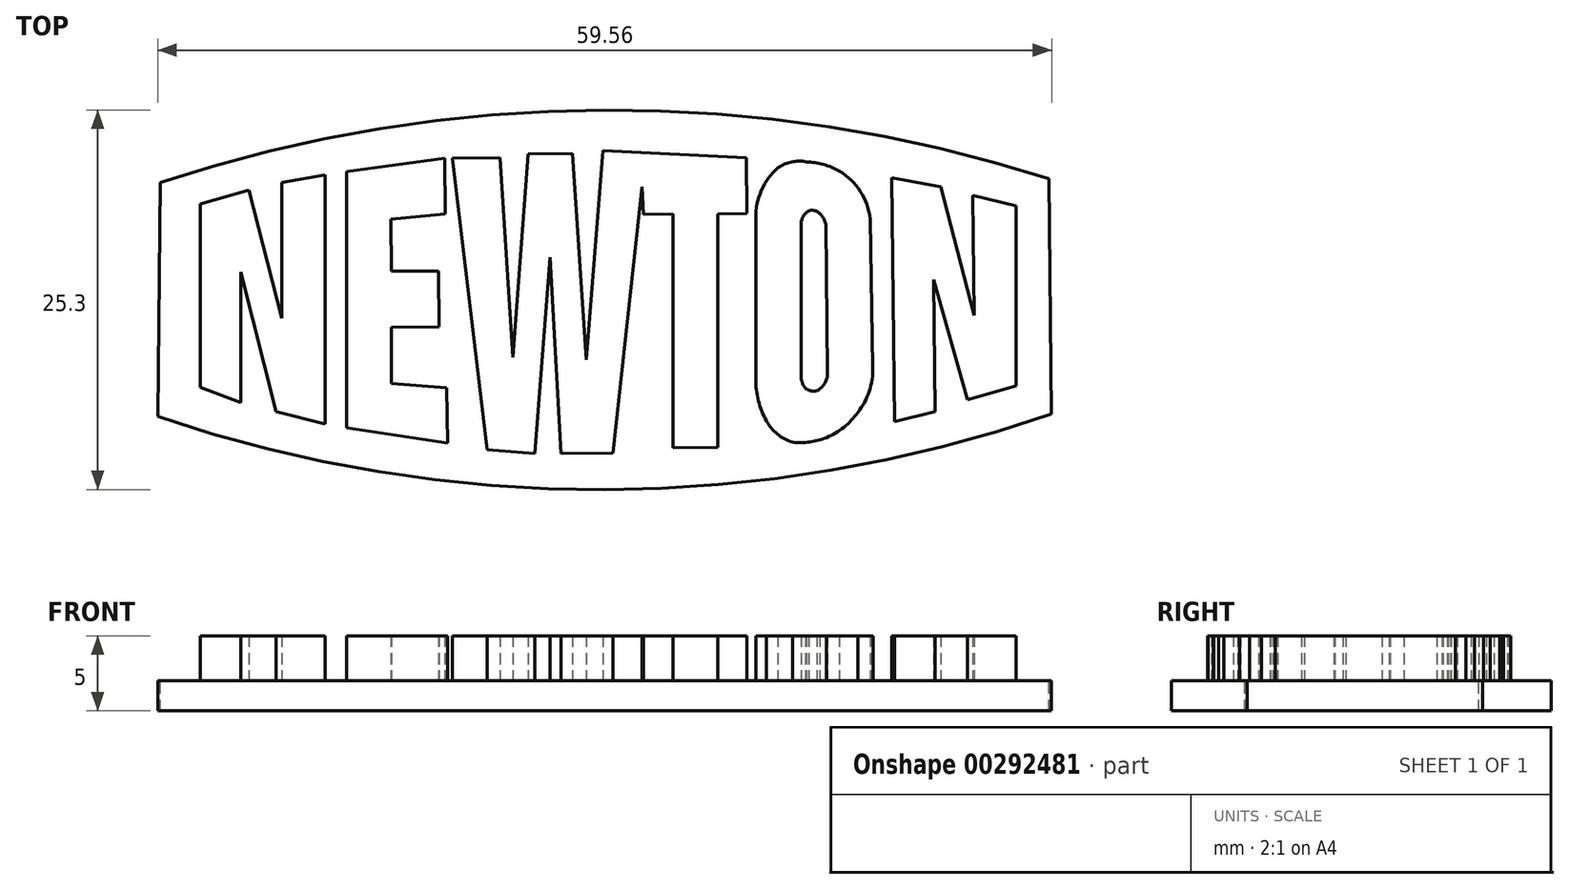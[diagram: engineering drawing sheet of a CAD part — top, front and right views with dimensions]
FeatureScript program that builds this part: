
annotation { "Feature Type Name" : "Feature", "Feature Type Description" : "" }
export const myFeature = defineFeature(function(context is Context, id is Id, definition is map)
    precondition{}
    {
        {
            var Q0;
            Q0=qCreatedBy(makeId("Top.planeOp"),FACE);
            var sketch = newSketch(context, id + "F0", { "sketchPlane" : qUnion([Q0])});
            skLineSegment(sketch, "E0", {"start": v(-26.81, 7.81) * mm, "end": v(-26.81, -4.43) * mm});
            skLineSegment(sketch, "E1", {"start": v(-26.81, -4.43) * mm, "end": v(-24.1, -5.44) * mm});
            skLineSegment(sketch, "E2", {"start": v(-24.1, -5.44) * mm, "end": v(-24.1, 3.27) * mm});
            skLineSegment(sketch, "E3", {"start": v(-24.1, 3.27) * mm, "end": v(-21.76, -6.03) * mm});
            skLineSegment(sketch, "E4", {"start": v(-21.76, -6.03) * mm, "end": v(-18.5, -6.85) * mm});
            skLineSegment(sketch, "E5", {"start": v(-18.5, -6.85) * mm, "end": v(-18.5, 9.74) * mm});
            skLineSegment(sketch, "E6", {"start": v(-18.5, 9.74) * mm, "end": v(-21.37, 9.23) * mm});
            skLineSegment(sketch, "E7", {"start": v(-21.37, 9.23) * mm, "end": v(-21.37, 0.18) * mm});
            skLineSegment(sketch, "E8", {"start": v(-21.37, 0.18) * mm, "end": v(-23.57, 8.73) * mm});
            skLineSegment(sketch, "E9", {"start": v(-23.57, 8.73) * mm, "end": v(-26.81, 7.81) * mm});
            skLineSegment(sketch, "E10", {"start": v(-17.06, 9.97) * mm, "end": v(-10.53, 10.85) * mm});
            skLineSegment(sketch, "E11", {"start": v(-10.53, 10.85) * mm, "end": v(-10.48, 7.13) * mm});
            skLineSegment(sketch, "E12", {"start": v(-10.48, 7.13) * mm, "end": v(-14.13, 6.8) * mm});
            skLineSegment(sketch, "E13", {"start": v(-14.13, 6.8) * mm, "end": v(-14.09, 3.32) * mm});
            skLineSegment(sketch, "E14", {"start": v(-14.09, 3.32) * mm, "end": v(-10.95, 3.32) * mm});
            skLineSegment(sketch, "E15", {"start": v(-10.95, 3.32) * mm, "end": v(-10.9, -0.37) * mm});
            skLineSegment(sketch, "E16", {"start": v(-10.9, -0.37) * mm, "end": v(-14.09, -0.4) * mm});
            skLineSegment(sketch, "E17", {"start": v(-14.09, -0.4) * mm, "end": v(-14.09, -4.17) * mm});
            skLineSegment(sketch, "E18", {"start": v(-14.09, -4.17) * mm, "end": v(-10.4, -4.45) * mm});
            skLineSegment(sketch, "E19", {"start": v(-10.4, -4.45) * mm, "end": v(-10.35, -8.14) * mm});
            skLineSegment(sketch, "E20", {"start": v(-10.35, -8.14) * mm, "end": v(-17.06, -7.12) * mm});
            skLineSegment(sketch, "E21", {"start": v(-17.06, -7.12) * mm, "end": v(-17.06, 9.97) * mm});
            skLineSegment(sketch, "E22", {"start": v(-10.01, 10.85) * mm, "end": v(-6.84, 10.89) * mm});
            skLineSegment(sketch, "E23", {"start": v(-6.84, 10.89) * mm, "end": v(-5.97, -2.4) * mm});
            skLineSegment(sketch, "E24", {"start": v(-5.97, -2.4) * mm, "end": v(-4.97, 11.15) * mm});
            skLineSegment(sketch, "E25", {"start": v(-4.97, 11.15) * mm, "end": v(-2.03, 11.19) * mm});
            skLineSegment(sketch, "E26", {"start": v(-2.03, 11.19) * mm, "end": v(-1.08, -2.57) * mm});
            skLineSegment(sketch, "E27", {"start": v(-1.08, -2.57) * mm, "end": v(0, 11.35) * mm});
            skLineSegment(sketch, "E28", {"start": v(0, 11.35) * mm, "end": v(9.57, 10.89) * mm});
            skLineSegment(sketch, "E29", {"start": v(9.57, 10.89) * mm, "end": v(9.61, 7.17) * mm});
            skLineSegment(sketch, "E30", {"start": v(9.61, 7.17) * mm, "end": v(7.66, 7.14) * mm});
            skLineSegment(sketch, "E31", {"start": v(7.66, 7.14) * mm, "end": v(7.66, -8.4) * mm});
            skLineSegment(sketch, "E32", {"start": v(7.66, -8.4) * mm, "end": v(4.68, -8.44) * mm});
            skLineSegment(sketch, "E33", {"start": v(4.68, -8.44) * mm, "end": v(4.68, 7.14) * mm});
            skLineSegment(sketch, "E34", {"start": v(4.68, 7.14) * mm, "end": v(2.7, 7.12) * mm});
            skLineSegment(sketch, "E35", {"start": v(2.7, 7.12) * mm, "end": v(2.62, 8.95) * mm});
            skLineSegment(sketch, "E36", {"start": v(2.62, 8.95) * mm, "end": v(0.68, -8.8) * mm});
            skLineSegment(sketch, "E37", {"start": v(0.68, -8.8) * mm, "end": v(-2.8, -8.83) * mm});
            skLineSegment(sketch, "E38", {"start": v(-2.8, -8.83) * mm, "end": v(-3.52, 4.25) * mm});
            skLineSegment(sketch, "E39", {"start": v(-3.52, 4.25) * mm, "end": v(-4.53, -8.83) * mm});
            skLineSegment(sketch, "E40", {"start": v(-4.53, -8.83) * mm, "end": v(-7.7, -8.59) * mm});
            skLineSegment(sketch, "E41", {"start": v(-7.7, -8.59) * mm, "end": v(-10.01, 10.85) * mm});
            skLineSegment(sketch, "E42", {"start": v(19.26, 9.55) * mm, "end": v(19.45, -6.7) * mm});
            skLineSegment(sketch, "E43", {"start": v(19.45, -6.7) * mm, "end": v(22.15, -6.04) * mm});
            skLineSegment(sketch, "E44", {"start": v(22.15, -6.04) * mm, "end": v(22.04, 2.78) * mm});
            skLineSegment(sketch, "E45", {"start": v(22.04, 2.78) * mm, "end": v(24.3, -5.24) * mm});
            skLineSegment(sketch, "E46", {"start": v(24.3, -5.24) * mm, "end": v(27.54, -4.32) * mm});
            skLineSegment(sketch, "E47", {"start": v(27.54, -4.32) * mm, "end": v(27.54, 7.68) * mm});
            skLineSegment(sketch, "E48", {"start": v(27.54, 7.68) * mm, "end": v(24.67, 8.38) * mm});
            skLineSegment(sketch, "E49", {"start": v(24.67, 8.38) * mm, "end": v(24.76, 0.38) * mm});
            skLineSegment(sketch, "E50", {"start": v(24.76, 0.38) * mm, "end": v(22.53, 8.96) * mm});
            skLineSegment(sketch, "E51", {"start": v(22.53, 8.96) * mm, "end": v(19.26, 9.55) * mm});
            skLineSegment(sketch, "E52", {"start": v(13.22, 6.44) * mm, "end": v(13.22, -3.66) * mm});
            skLineSegment(sketch, "E53", {"start": v(14.87, 6.44) * mm, "end": v(14.99, -3.43) * mm});
            skArc(sketch, "E54", {"start": v(13.72, 7.35) * mm, "mid": v(13.35, 6.96) * mm, "end": v(13.22, 6.44) * mm});
            skArc(sketch, "E55", {"start": v(14.45, 7.19) * mm, "mid": v(14.1, 7.37) * mm, "end": v(13.72, 7.35) * mm});
            skArc(sketch, "E56", {"start": v(14.87, 6.44) * mm, "mid": v(14.7, 6.84) * mm, "end": v(14.45, 7.19) * mm});
            skArc(sketch, "E57", {"start": v(11.68, 10.23) * mm, "mid": v(10.57, 8.7) * mm, "end": v(10.2, 6.86) * mm});
            skArc(sketch, "E58", {"start": v(13.56, 10.61) * mm, "mid": v(12.58, 10.61) * mm, "end": v(11.68, 10.23) * mm});
            skArc(sketch, "E59", {"start": v(16.39, 9.59) * mm, "mid": v(15.06, 10.33) * mm, "end": v(13.56, 10.61) * mm});
            skArc(sketch, "E60", {"start": v(17.83, 6.8) * mm, "mid": v(17.17, 8.64) * mm, "end": v(15.77, 10) * mm});
            skLineSegment(sketch, "E61", {"start": v(17.83, 6.8) * mm, "end": v(18, -3.08) * mm});
            skLineSegment(sketch, "E62", {"start": v(10.2, -3.86) * mm, "end": v(10.2, 6.86) * mm});
            skArc(sketch, "E63", {"start": v(10.2, -3.86) * mm, "mid": v(10.37, -5.3) * mm, "end": v(10.9, -6.64) * mm});
            skArc(sketch, "E64", {"start": v(10.9, -6.64) * mm, "mid": v(11.64, -7.53) * mm, "end": v(12.66, -8.08) * mm});
            skArc(sketch, "E65", {"start": v(12.66, -8.08) * mm, "mid": v(13.8, -8.05) * mm, "end": v(14.9, -7.77) * mm});
            skArc(sketch, "E66", {"start": v(14.9, -7.77) * mm, "mid": v(16.07, -7.07) * mm, "end": v(17, -6.08) * mm});
            skArc(sketch, "E67", {"start": v(17, -6.08) * mm, "mid": v(17.76, -4.67) * mm, "end": v(18, -3.08) * mm});
            skArc(sketch, "E68", {"start": v(13.22, -3.66) * mm, "mid": v(13.3, -4.1) * mm, "end": v(13.5, -4.48) * mm});
            skArc(sketch, "E69", {"start": v(13.5, -4.48) * mm, "mid": v(13.87, -4.65) * mm, "end": v(14.28, -4.64) * mm});
            skArc(sketch, "E70", {"start": v(14.28, -4.64) * mm, "mid": v(14.8, -4.13) * mm, "end": v(14.99, -3.43) * mm});
            skSolve(sketch);
        }
        {
            var Q0;
            Q0 = qSketchRegion(id + "F0", true);
            extrude(context, id + "F1", {"entities" : qUnion([Q0]), "depth" : 3 * mm});
        }
        {
            var Q0;
            Q0=makeQuery(id+"F1.opExtrude","CAP_FACE",FACE,{"disambiguationData":[OSD([sQuery(id+"F0.wireOp",EDGE,"k1h50pG2-Ytod-GWjl-Ulda-jVNFQqZc98Fo"),sQuery(id+"F0.wireOp",EDGE,"AT3KaTZv-xVJ6-UHdJ-6nbH-usGnLGP7IWQC"),sQuery(id+"F0.wireOp",EDGE,"bRftn0zI-Tklm-IMop-Rnqt-7tXfIlYmBiHp"),sQuery(id+"F0.wireOp",EDGE,"3HuRXAhB-mzyN-2NtB-xwSD-R41m3GkumpOy"),sQuery(id+"F0.wireOp",EDGE,"E0"),sQuery(id+"F0.wireOp",EDGE,"E1"),sQuery(id+"F0.wireOp",EDGE,"E2"),sQuery(id+"F0.wireOp",EDGE,"E3"),sQuery(id+"F0.wireOp",EDGE,"E4"),sQuery(id+"F0.wireOp",EDGE,"E5"),sQuery(id+"F0.wireOp",EDGE,"E6"),sQuery(id+"F0.wireOp",EDGE,"E7"),sQuery(id+"F0.wireOp",EDGE,"E8"),sQuery(id+"F0.wireOp",EDGE,"E9"),sQuery(id+"F0.wireOp",EDGE,"E10"),sQuery(id+"F0.wireOp",EDGE,"E11"),sQuery(id+"F0.wireOp",EDGE,"E12"),sQuery(id+"F0.wireOp",EDGE,"E13"),sQuery(id+"F0.wireOp",EDGE,"E14"),sQuery(id+"F0.wireOp",EDGE,"E15"),sQuery(id+"F0.wireOp",EDGE,"E16"),sQuery(id+"F0.wireOp",EDGE,"E17"),sQuery(id+"F0.wireOp",EDGE,"E18"),sQuery(id+"F0.wireOp",EDGE,"E19"),sQuery(id+"F0.wireOp",EDGE,"E20"),sQuery(id+"F0.wireOp",EDGE,"E21"),sQuery(id+"F0.wireOp",EDGE,"E22"),sQuery(id+"F0.wireOp",EDGE,"E23"),sQuery(id+"F0.wireOp",EDGE,"E24"),sQuery(id+"F0.wireOp",EDGE,"E25"),sQuery(id+"F0.wireOp",EDGE,"E26"),sQuery(id+"F0.wireOp",EDGE,"E27"),sQuery(id+"F0.wireOp",EDGE,"E28"),sQuery(id+"F0.wireOp",EDGE,"E29"),sQuery(id+"F0.wireOp",EDGE,"E30"),sQuery(id+"F0.wireOp",EDGE,"E31"),sQuery(id+"F0.wireOp",EDGE,"E32"),sQuery(id+"F0.wireOp",EDGE,"E33"),sQuery(id+"F0.wireOp",EDGE,"E34"),sQuery(id+"F0.wireOp",EDGE,"E35"),sQuery(id+"F0.wireOp",EDGE,"E36"),sQuery(id+"F0.wireOp",EDGE,"E37"),sQuery(id+"F0.wireOp",EDGE,"E38"),sQuery(id+"F0.wireOp",EDGE,"E39"),sQuery(id+"F0.wireOp",EDGE,"E40"),sQuery(id+"F0.wireOp",EDGE,"E41"),sQuery(id+"F0.wireOp",EDGE,"E42"),sQuery(id+"F0.wireOp",EDGE,"E43"),sQuery(id+"F0.wireOp",EDGE,"E44"),sQuery(id+"F0.wireOp",EDGE,"E45"),sQuery(id+"F0.wireOp",EDGE,"E46"),sQuery(id+"F0.wireOp",EDGE,"E47"),sQuery(id+"F0.wireOp",EDGE,"E48"),sQuery(id+"F0.wireOp",EDGE,"E49"),sQuery(id+"F0.wireOp",EDGE,"E50"),sQuery(id+"F0.wireOp",EDGE,"E51"),sQuery(id+"F0.wireOp",EDGE,"E57"),sQuery(id+"F0.wireOp",EDGE,"E58"),sQuery(id+"F0.wireOp",EDGE,"E59"),sQuery(id+"F0.wireOp",EDGE,"E60"),sQuery(id+"F0.wireOp",EDGE,"E61"),sQuery(id+"F0.wireOp",EDGE,"E62"),sQuery(id+"F0.wireOp",EDGE,"E63"),sQuery(id+"F0.wireOp",EDGE,"E64"),sQuery(id+"F0.wireOp",EDGE,"E65"),sQuery(id+"F0.wireOp",EDGE,"E66"),sQuery(id+"F0.wireOp",EDGE,"E67")])],"isStart":true});
            var sketch = newSketch(context, id + "F2", { "sketchPlane" : qUnion([Q0])});
            skArc(sketch, "E71", {"start": v(29.9, 6.18) * mm, "mid": v(0.14, 11.23) * mm, "end": v(-29.65, 6.37) * mm});
            skLineSegment(sketch, "E72", {"start": v(-29.65, 6.37) * mm, "end": v(-29.47, -9.23) * mm});
            skArc(sketch, "E73", {"start": v(-29.47, -9.23) * mm, "mid": v(0.1, -14.07) * mm, "end": v(29.73, -9.5) * mm});
            skLineSegment(sketch, "E74", {"start": v(29.9, 6.18) * mm, "end": v(29.73, -9.5) * mm});
            skSolve(sketch);
        }
        {
            var Q0;
            Q0 = qSketchRegion(id + "F2", true);
            extrude(context, id + "F3", {"entities" : qUnion([Q0]), "operationType" : NewBodyOperationType.ADD, "depth" : 2 * mm});
        }
    });
